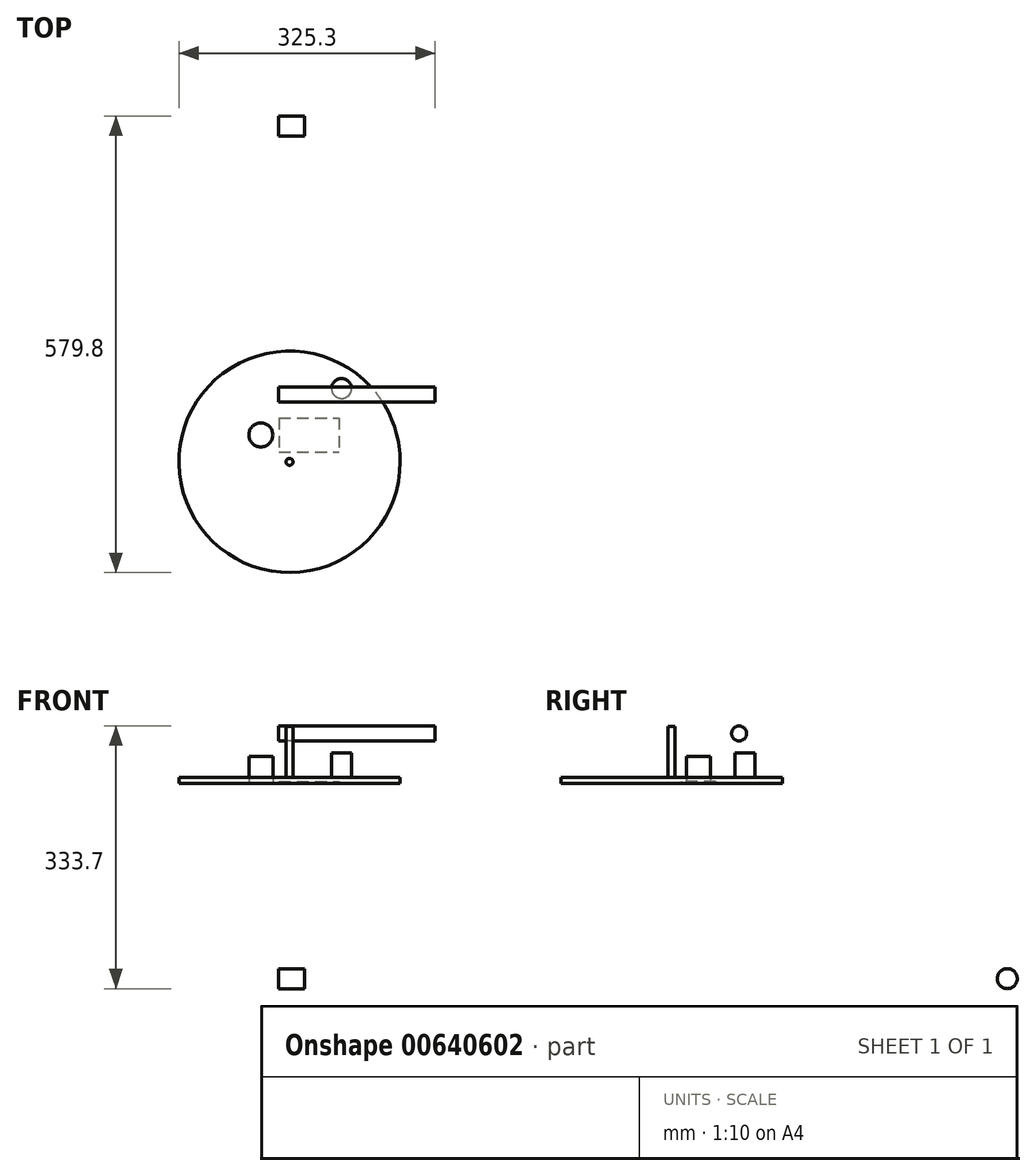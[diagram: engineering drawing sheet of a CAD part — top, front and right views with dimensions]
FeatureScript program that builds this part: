
annotation { "Feature Type Name" : "Feature", "Feature Type Description" : "" }
export const myFeature = defineFeature(function(context is Context, id is Id, definition is map)
    precondition{}
    {
        {
            var Q0;
            Q0=qCreatedBy(makeId("Top.planeOp"),FACE);
            var sketch = newSketch(context, id + "F0", { "sketchPlane" : qUnion([Q0])});
            skCircle(sketch, "E0", {"center": v(-22.54, 9.78) * mm, "radius": 15.24 * mm});
            skSolve(sketch);
        }
        {
            var Q0;
            Q0=makeQuery(id+"F0.imprint","IMPRINT",FACE,{"disambiguationData":[TD([[makeQuery(id+"F0.imprint","IMPRINT",EDGE,{"derivedFrom":sQuery(id+"F0.wireOp",EDGE,"E0")}),1.0]])]});
            extrude(context, id + "F1", {"entities" : qUnion([Q0]), "depth" : 34.3 * mm, "offsetDistance" : 25.4 * mm});
        }
        {
            var Q0;
            Q0=qCreatedBy(makeId("Top.planeOp"),FACE);
            var sketch = newSketch(context, id + "F2", { "sketchPlane" : qUnion([Q0])});
            skLineSegment(sketch, "E1.bottom", {"start": v(0.37, 31.47) * mm, "end": v(76.57, 31.47) * mm});
            skLineSegment(sketch, "E1.top", {"start": v(0.37, -11.66) * mm, "end": v(76.57, -11.66) * mm});
            skLineSegment(sketch, "E1.left", {"start": v(0.37, 31.47) * mm, "end": v(0.37, -11.66) * mm});
            skLineSegment(sketch, "E1.right", {"start": v(76.57, 31.47) * mm, "end": v(76.57, -11.66) * mm});
            skSolve(sketch);
        }
        {
            var Q0;
            Q0=makeQuery(id+"F2.imprint","IMPRINT",FACE,{"disambiguationData":[TD([[makeQuery(id+"F2.imprint","IMPRINT",EDGE,{"derivedFrom":sQuery(id+"F2.wireOp",EDGE,"E1.bottom")}),-1.0]])]});
            extrude(context, id + "F3", {"entities" : qUnion([Q0]), "depth" : 2.3 * mm, "offsetDistance" : 25.4 * mm});
        }
        {
            var Q0;
            Q0=qCreatedBy(makeId("Top.planeOp"),FACE);
            var sketch = newSketch(context, id + "F4", { "sketchPlane" : qUnion([Q0])});
            skCircle(sketch, "E2", {"center": v(13.91, -24.43) * mm, "radius": 140.58 * mm});
            skSolve(sketch);
        }
        {
            var Q0;
            Q0=makeQuery(id+"F4.imprint","IMPRINT",FACE,{"disambiguationData":[TD([[makeQuery(id+"F4.imprint","IMPRINT",EDGE,{"derivedFrom":sQuery(id+"F4.wireOp",EDGE,"E2")}),1.0]])]});
            extrude(context, id + "F5", {"entities" : qUnion([Q0]), "depth" : 7.62 * mm, "offsetDistance" : 25.4 * mm});
        }
        {
            var Q0;
            Q0=qCreatedBy(makeId("Right.planeOp"),FACE);
            var sketch = newSketch(context, id + "F6", { "sketchPlane" : qUnion([Q0])});
            skCircle(sketch, "E3", {"center": v(61.3, 63.16) * mm, "radius": 9.53 * mm});
            skSolve(sketch);
        }
        {
            var Q0;
            Q0 = qSketchRegion(id + "F6", true);
            extrude(context, id + "F7", {"entities" : qUnion([Q0]), "depth" : 198.63 * mm, "offsetDistance" : 25.4 * mm});
        }
        {
            var Q0;
            Q0=makeQuery(id+"F5.opExtrude","CAP_FACE",FACE,{"disambiguationData":[OSD([sQuery(id+"F4.wireOp",EDGE,"E2")])],"isStart":false});
            var sketch = newSketch(context, id + "F8", { "sketchPlane" : qUnion([Q0])});
            skLineSegment(sketch, "E4", {"start": v(-51.64, 127.67) * mm, "end": v(-131.59, 127.67) * mm});
            skCircle(sketch, "E5", {"center": v(13.91, -24.43) * mm, "radius": 4.48 * mm});
            skSolve(sketch);
        }
        {
            var Q0;
            Q0=makeQuery(id+"F7.opExtrude","CAP_FACE",FACE,{"disambiguationData":[OSD([sQuery(id+"F6.wireOp",EDGE,"E3")])],"isStart":true});
            var sketch = newSketch(context, id + "F9", { "sketchPlane" : qUnion([Q0])});
            skCircle(sketch, "E6", {"center": v(-402.09, -248.32) * mm, "radius": 12.7 * mm});
            skSolve(sketch);
        }
        {
            var Q0;
            Q0=makeQuery(id+"F9.imprint","IMPRINT",FACE,{"disambiguationData":[TD([[makeQuery(id+"F9.imprint","IMPRINT",EDGE,{"derivedFrom":sQuery(id+"F9.wireOp",EDGE,"E6")}),1.0]])]});
            extrude(context, id + "F10", {"entities" : qUnion([Q0]), "oppositeDirection" : true, "depth" : 33.02 * mm, "offsetDistance" : 25.4 * mm});
        }
        {
            var Q0;
            Q0=makeQuery(id+"F8.imprint","IMPRINT",FACE,{"disambiguationData":[TD([[makeQuery(id+"F8.imprint","IMPRINT",EDGE,{"derivedFrom":makeQuery(id+"F5.opExtrude","CAP_EDGE",EDGE,{"disambiguationData":[OSD([sQuery(id+"F4.wireOp",EDGE,"E2")])],"isStart":false})}),1.0]])]});
            var sketch = newSketch(context, id + "F11", { "sketchPlane" : qUnion([Q0])});
            skCircle(sketch, "E7", {"center": v(79.96, 68.75) * mm, "radius": 12.7 * mm});
            skSolve(sketch);
        }
        {
            var Q0;
            Q0 = qSketchRegion(id + "F11", true);
            extrude(context, id + "F12", {"entities" : qUnion([Q0]), "operationType" : NewBodyOperationType.ADD, "depth" : 30.99 * mm, "offsetDistance" : 25.4 * mm});
        }
        {
            var Q0;
            Q0=makeQuery(id+"F8.imprint","IMPRINT",FACE,{"disambiguationData":[TD([[makeQuery(id+"F8.imprint","IMPRINT",EDGE,{"derivedFrom":sQuery(id+"F8.wireOp",EDGE,"E5")}),1.0]])]});
            extrude(context, id + "F13", {"entities" : qUnion([Q0]), "operationType" : NewBodyOperationType.ADD, "depth" : 64.52 * mm, "offsetDistance" : 25.4 * mm});
        }
    });
